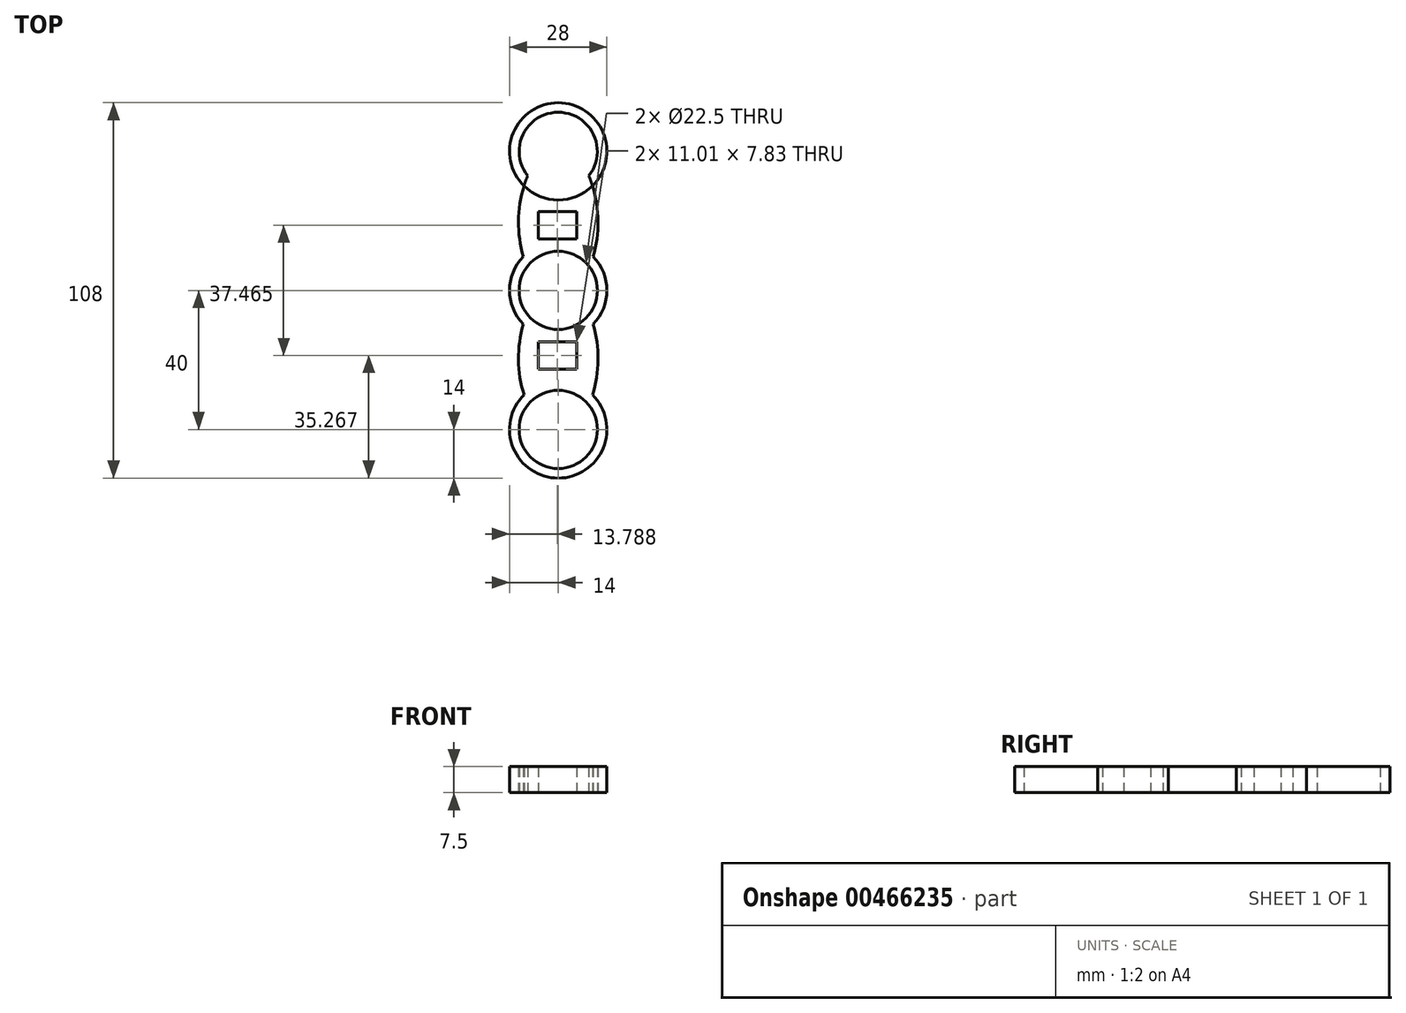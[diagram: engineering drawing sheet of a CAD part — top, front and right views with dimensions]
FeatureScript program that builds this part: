
annotation { "Feature Type Name" : "Feature", "Feature Type Description" : "" }
export const myFeature = defineFeature(function(context is Context, id is Id, definition is map)
    precondition{}
    {
        {
            var Q0;
            Q0=qCreatedBy(makeId("Top.planeOp"),FACE);
            var sketch = newSketch(context, id + "F0", { "sketchPlane" : qUnion([Q0])});
            skCircle(sketch, "E0", {"center": v(0, 0) * mm, "radius": 11.25 * mm});
            skLineSegment(sketch, "E1", {"start": v(0, 0) * mm, "end": v(0, 40) * mm});
            skLineSegment(sketch, "E2", {"start": v(0, 40) * mm, "end": v(0, 0) * mm});
            skLineSegment(sketch, "E3", {"start": v(0, 0) * mm, "end": v(0, -40) * mm});
            skCircle(sketch, "E4", {"center": v(0, 40) * mm, "radius": 11.25 * mm});
            skCircle(sketch, "E5", {"center": v(0, -40) * mm, "radius": 11.25 * mm});
            skLineSegment(sketch, "E6", {"start": v(0, 0) * mm, "end": v(-41.49, 0) * mm});
            skLineSegment(sketch, "E7", {"start": v(-41.49, 0) * mm, "end": v(0, 0) * mm});
            skLineSegment(sketch, "E8", {"start": v(38.1, 0) * mm, "end": v(0, 0) * mm});
            skArc(sketch, "E9", {"start": v(-5.08, 39.8) * mm, "mid": v(-11.44, 19.96) * mm, "end": v(-5.5, 0) * mm});
            skArc(sketch, "E10.MirrorCS", {"start": v(5.08, 39.8) * mm, "mid": v(11.44, 19.96) * mm, "end": v(5.5, 0) * mm});
            skArc(sketch, "E11.MirrorCS", {"start": v(-5.08, -39.8) * mm, "mid": v(-11.44, -19.96) * mm, "end": v(-5.5, 0) * mm});
            skArc(sketch, "E12.MirrorCS", {"start": v(5.08, -39.8) * mm, "mid": v(11.44, -19.96) * mm, "end": v(5.5, 0) * mm});
            skCircle(sketch, "E13", {"center": v(0, 40) * mm, "radius": 14 * mm});
            skCircle(sketch, "E14", {"center": v(0, 0) * mm, "radius": 14 * mm});
            skCircle(sketch, "E15", {"center": v(0, -40) * mm, "radius": 14 * mm});
            skLineSegment(sketch, "E16.bottom", {"start": v(-5.72, 22.65) * mm, "end": v(5.3, 22.65) * mm});
            skLineSegment(sketch, "E16.top", {"start": v(-5.72, 14.82) * mm, "end": v(5.3, 14.82) * mm});
            skLineSegment(sketch, "E16.left", {"start": v(-5.72, 22.65) * mm, "end": v(-5.72, 14.82) * mm});
            skLineSegment(sketch, "E16.right", {"start": v(5.3, 22.65) * mm, "end": v(5.3, 14.82) * mm});
            skLineSegment(sketch, "E17.MirrorCS", {"start": v(-5.72, -22.65) * mm, "end": v(-5.72, -14.82) * mm});
            skLineSegment(sketch, "E18.MirrorCS", {"start": v(-5.72, -22.65) * mm, "end": v(5.3, -22.65) * mm});
            skLineSegment(sketch, "E19.MirrorCS", {"start": v(5.3, -22.65) * mm, "end": v(5.3, -14.82) * mm});
            skLineSegment(sketch, "E20.MirrorCS", {"start": v(-5.72, -14.82) * mm, "end": v(5.3, -14.82) * mm});
            skSolve(sketch);
        }
        {
            var Q0;
            {var subQ0=sQuery(id+"F0.wireOp",EDGE,"E9");var subQ1=sQuery(id+"F0.wireOp",EDGE,"E4");var subQ2=makeQuery(id+"F0.imprint","INTERSECT",VERTEX,{"derivedFrom":[subQ1,subQ0]});Q0=makeQuery(id+"F0.imprint","IMPRINT",FACE,{"disambiguationData":[TD([[makeQuery(id+"F0.imprint","IMPRINT",EDGE,{"disambiguationData":[TD([[subQ2,1.0]])],"derivedFrom":subQ1}),-1.0]])]});}
            var Q1;
            {var subQ0=sQuery(id+"F0.wireOp",EDGE,"E4");var subQ1=sQuery(id+"F0.wireOp",EDGE,"E2");var subQ2=makeQuery(id+"F0.imprint","INTERSECT",VERTEX,{"derivedFrom":[subQ1,subQ0]});Q1=makeQuery(id+"F0.imprint","IMPRINT",FACE,{"disambiguationData":[TD([[makeQuery(id+"F0.imprint","IMPRINT",EDGE,{"disambiguationData":[TD([[subQ2,-1.0]])],"derivedFrom":subQ1}),-1.0]])]});}
            var Q2;
            {var subQ0=sQuery(id+"F0.wireOp",EDGE,"E4");var subQ1=sQuery(id+"F0.wireOp",EDGE,"E2");var subQ2=makeQuery(id+"F0.imprint","INTERSECT",VERTEX,{"derivedFrom":[subQ1,subQ0]});Q2=makeQuery(id+"F0.imprint","IMPRINT",FACE,{"disambiguationData":[TD([[makeQuery(id+"F0.imprint","IMPRINT",EDGE,{"disambiguationData":[TD([[subQ2,-1.0]])],"derivedFrom":subQ1}),1.0]])]});}
            var Q3;
            {var subQ12=sQuery(id+"F0.wireOp",EDGE,"E16.right");Q3=makeQuery(id+"F0.imprint","IMPRINT",FACE,{"disambiguationData":[TD([[makeQuery(id+"F0.imprint","IMPRINT",EDGE,{"derivedFrom":subQ12}),1.0]])]});}
            var Q4;
            {var subQ10=sQuery(id+"F0.wireOp",EDGE,"E16.left");Q4=makeQuery(id+"F0.imprint","IMPRINT",FACE,{"disambiguationData":[TD([[makeQuery(id+"F0.imprint","IMPRINT",EDGE,{"derivedFrom":subQ10}),-1.0]])]});}
            var Q5;
            {var subQ0=sQuery(id+"F0.wireOp",EDGE,"E10.MirrorCS");var subQ1=sQuery(id+"F0.wireOp",EDGE,"E0");var subQ2=makeQuery(id+"F0.imprint","INTERSECT",VERTEX,{"derivedFrom":[subQ1,subQ0]});Q5=makeQuery(id+"F0.imprint","IMPRINT",FACE,{"disambiguationData":[TD([[makeQuery(id+"F0.imprint","IMPRINT",EDGE,{"disambiguationData":[TD([[subQ2,-1.0]])],"derivedFrom":subQ1}),-1.0]])]});}
            var Q6;
            {var subQ0=sQuery(id+"F0.wireOp",EDGE,"E10.MirrorCS");var subQ1=sQuery(id+"F0.wireOp",EDGE,"E0");var subQ2=makeQuery(id+"F0.imprint","INTERSECT",VERTEX,{"derivedFrom":[subQ1,subQ0]});Q6=makeQuery(id+"F0.imprint","IMPRINT",FACE,{"disambiguationData":[TD([[makeQuery(id+"F0.imprint","IMPRINT",EDGE,{"disambiguationData":[TD([[subQ2,1.0]])],"derivedFrom":subQ1}),-1.0]])]});}
            var Q7;
            {var subQ0=sQuery(id+"F0.wireOp",EDGE,"E2");var subQ1=sQuery(id+"F0.wireOp",EDGE,"E0");var subQ2=makeQuery(id+"F0.imprint","INTERSECT",VERTEX,{"derivedFrom":[subQ1,subQ0]});Q7=makeQuery(id+"F0.imprint","IMPRINT",FACE,{"disambiguationData":[TD([[makeQuery(id+"F0.imprint","IMPRINT",EDGE,{"disambiguationData":[TD([[subQ2,-1.0]])],"derivedFrom":subQ1}),-1.0]])]});}
            var Q8;
            {var subQ0=sQuery(id+"F0.wireOp",EDGE,"E9");var subQ1=sQuery(id+"F0.wireOp",EDGE,"E0");var subQ2=makeQuery(id+"F0.imprint","INTERSECT",VERTEX,{"derivedFrom":[subQ1,subQ0]});Q8=makeQuery(id+"F0.imprint","IMPRINT",FACE,{"disambiguationData":[TD([[makeQuery(id+"F0.imprint","IMPRINT",EDGE,{"disambiguationData":[TD([[subQ2,-1.0]])],"derivedFrom":subQ1}),-1.0]])]});}
            var Q9;
            {var subQ0=sQuery(id+"F0.wireOp",EDGE,"E7");var subQ1=sQuery(id+"F0.wireOp",EDGE,"E0");var subQ2=makeQuery(id+"F0.imprint","INTERSECT",VERTEX,{"derivedFrom":[subQ1,subQ0]});Q9=makeQuery(id+"F0.imprint","IMPRINT",FACE,{"disambiguationData":[TD([[makeQuery(id+"F0.imprint","IMPRINT",EDGE,{"disambiguationData":[TD([[subQ2,-1.0]])],"derivedFrom":subQ1}),-1.0]])]});}
            var Q10;
            {var subQ0=sQuery(id+"F0.wireOp",EDGE,"E8");var subQ1=sQuery(id+"F0.wireOp",EDGE,"E0");var subQ2=makeQuery(id+"F0.imprint","INTERSECT",VERTEX,{"derivedFrom":[subQ1,subQ0]});Q10=makeQuery(id+"F0.imprint","IMPRINT",FACE,{"disambiguationData":[TD([[makeQuery(id+"F0.imprint","IMPRINT",EDGE,{"disambiguationData":[TD([[subQ2,1.0]])],"derivedFrom":subQ1}),-1.0]])]});}
            var Q11;
            {var subQ0=sQuery(id+"F0.wireOp",EDGE,"E3");var subQ1=sQuery(id+"F0.wireOp",EDGE,"E0");var subQ2=makeQuery(id+"F0.imprint","INTERSECT",VERTEX,{"derivedFrom":[subQ1,subQ0]});Q11=makeQuery(id+"F0.imprint","IMPRINT",FACE,{"disambiguationData":[TD([[makeQuery(id+"F0.imprint","IMPRINT",EDGE,{"disambiguationData":[TD([[subQ2,-1.0]])],"derivedFrom":subQ1}),-1.0]])]});}
            var Q12;
            {var subQ0=sQuery(id+"F0.wireOp",EDGE,"E11.MirrorCS");var subQ1=sQuery(id+"F0.wireOp",EDGE,"E0");var subQ2=makeQuery(id+"F0.imprint","INTERSECT",VERTEX,{"derivedFrom":[subQ1,subQ0]});Q12=makeQuery(id+"F0.imprint","IMPRINT",FACE,{"disambiguationData":[TD([[makeQuery(id+"F0.imprint","IMPRINT",EDGE,{"disambiguationData":[TD([[subQ2,-1.0]])],"derivedFrom":subQ1}),-1.0]])]});}
            var Q13;
            {var subQ12=sQuery(id+"F0.wireOp",EDGE,"E17.MirrorCS");Q13=makeQuery(id+"F0.imprint","IMPRINT",FACE,{"disambiguationData":[TD([[makeQuery(id+"F0.imprint","IMPRINT",EDGE,{"derivedFrom":subQ12}),1.0]])]});}
            var Q14;
            {var subQ11=sQuery(id+"F0.wireOp",EDGE,"E19.MirrorCS");Q14=makeQuery(id+"F0.imprint","IMPRINT",FACE,{"disambiguationData":[TD([[makeQuery(id+"F0.imprint","IMPRINT",EDGE,{"derivedFrom":subQ11}),-1.0]])]});}
            var Q15;
            {var subQ0=sQuery(id+"F0.wireOp",EDGE,"E12.MirrorCS");var subQ1=sQuery(id+"F0.wireOp",EDGE,"E5");var subQ2=makeQuery(id+"F0.imprint","INTERSECT",VERTEX,{"derivedFrom":[subQ1,subQ0]});Q15=makeQuery(id+"F0.imprint","IMPRINT",FACE,{"disambiguationData":[TD([[makeQuery(id+"F0.imprint","IMPRINT",EDGE,{"disambiguationData":[TD([[subQ2,1.0]])],"derivedFrom":subQ1}),-1.0]])]});}
            var Q16;
            {var subQ0=sQuery(id+"F0.wireOp",EDGE,"E5");var subQ1=sQuery(id+"F0.wireOp",EDGE,"E3");var subQ2=makeQuery(id+"F0.imprint","INTERSECT",VERTEX,{"derivedFrom":[subQ1,subQ0]});Q16=makeQuery(id+"F0.imprint","IMPRINT",FACE,{"disambiguationData":[TD([[makeQuery(id+"F0.imprint","IMPRINT",EDGE,{"disambiguationData":[TD([[subQ2,1.0]])],"derivedFrom":subQ1}),-1.0]])]});}
            var Q17;
            {var subQ0=sQuery(id+"F0.wireOp",EDGE,"E5");var subQ1=sQuery(id+"F0.wireOp",EDGE,"E3");var subQ2=makeQuery(id+"F0.imprint","INTERSECT",VERTEX,{"derivedFrom":[subQ1,subQ0]});Q17=makeQuery(id+"F0.imprint","IMPRINT",FACE,{"disambiguationData":[TD([[makeQuery(id+"F0.imprint","IMPRINT",EDGE,{"disambiguationData":[TD([[subQ2,1.0]])],"derivedFrom":subQ1}),1.0]])]});}
            extrude(context, id + "F1", {"entities" : qUnion([Q0, Q1, Q2, Q3, Q4, Q5, Q6, Q7, Q8, Q9, Q10, Q11, Q12, Q13, Q14, Q15, Q16, Q17]), "depth" : 7.5 * mm});
        }
    });
